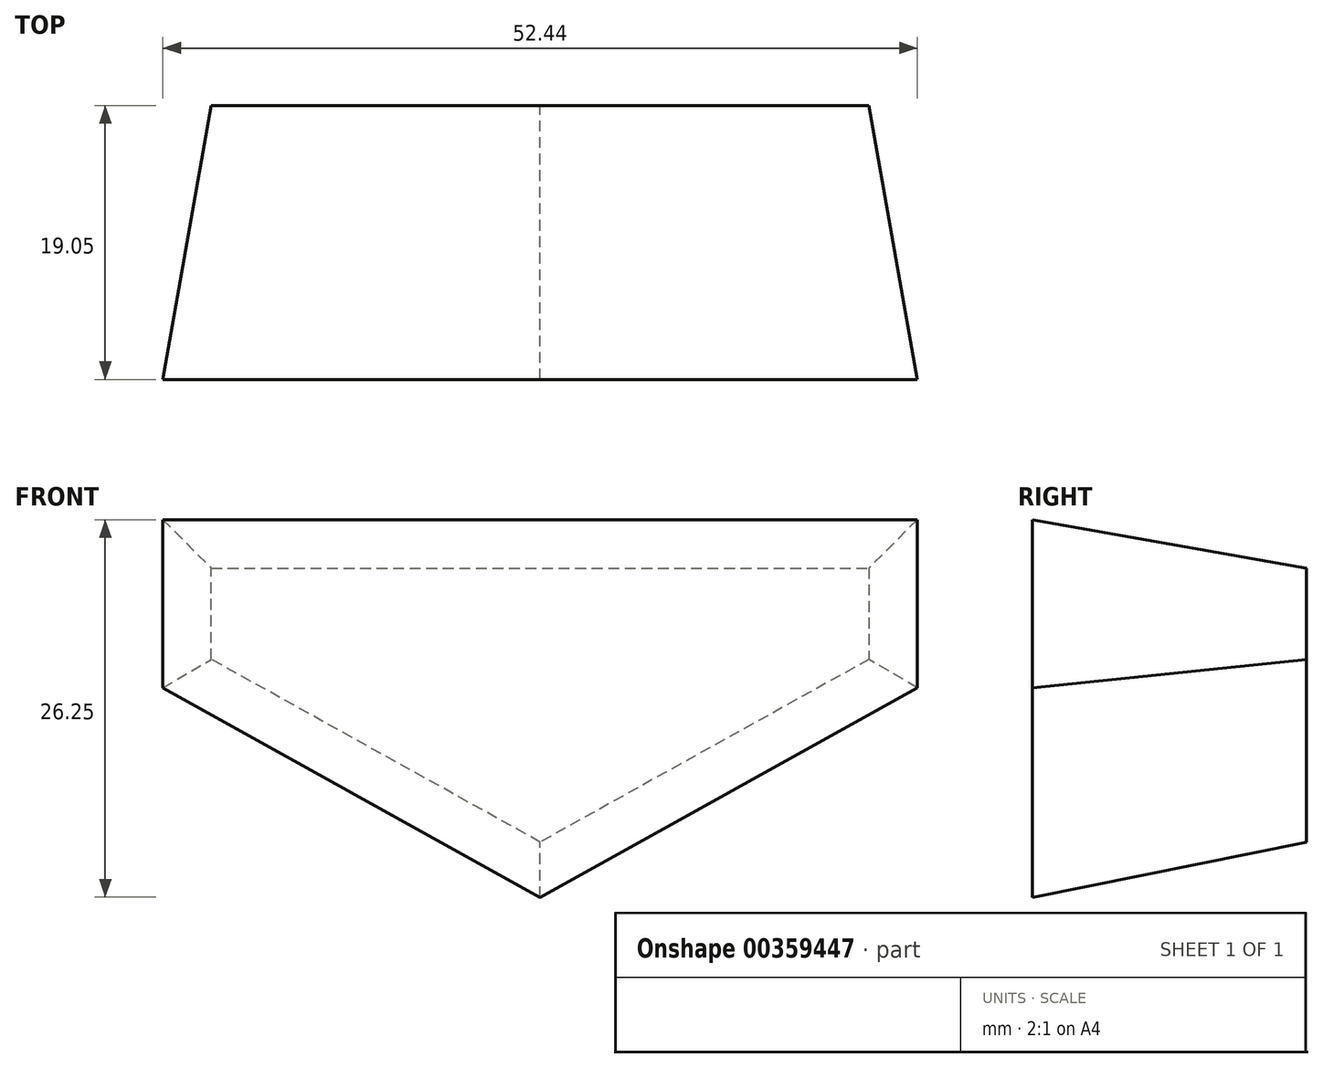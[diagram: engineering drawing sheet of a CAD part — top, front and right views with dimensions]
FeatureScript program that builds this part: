
annotation { "Feature Type Name" : "Feature", "Feature Type Description" : "" }
export const myFeature = defineFeature(function(context is Context, id is Id, definition is map)
    precondition{}
    {
        {
            var Q0;
            Q0=qCreatedBy(makeId("Front.planeOp"),FACE);
            var sketch = newSketch(context, id + "F0", { "sketchPlane" : qUnion([Q0])});
            skLineSegment(sketch, "E0", {"start": v(-16.54, 0) * mm, "end": v(29.18, 0) * mm});
            skLineSegment(sketch, "E1", {"start": v(29.18, 0) * mm, "end": v(29.18, -6.35) * mm});
            skLineSegment(sketch, "E2", {"start": v(29.18, -6.35) * mm, "end": v(6.32, -19.05) * mm});
            skPoint(sketch, "E2.endSnap0", {"position": v(6.32, 0) * mm});
            skLineSegment(sketch, "E3", {"start": v(6.32, -19.05) * mm, "end": v(-16.54, -6.35) * mm});
            skLineSegment(sketch, "E4", {"start": v(-16.54, -6.35) * mm, "end": v(-16.54, 0) * mm});
            skLineSegment(sketch, "E5", {"start": v(6.32, 0) * mm, "end": v(6.32, -19.05) * mm});
            skSolve(sketch);
        }
        {
            var Q0;
            Q0 = qSketchRegion(id + "F0", true);
            extrude(context, id + "F1", {"entities" : qUnion([Q0]), "depth" : 19.05 * mm, "offsetDistance" : 25.4 * mm, "hasDraft" : true, "draftAngle" : 10 * degree});
        }
    });
